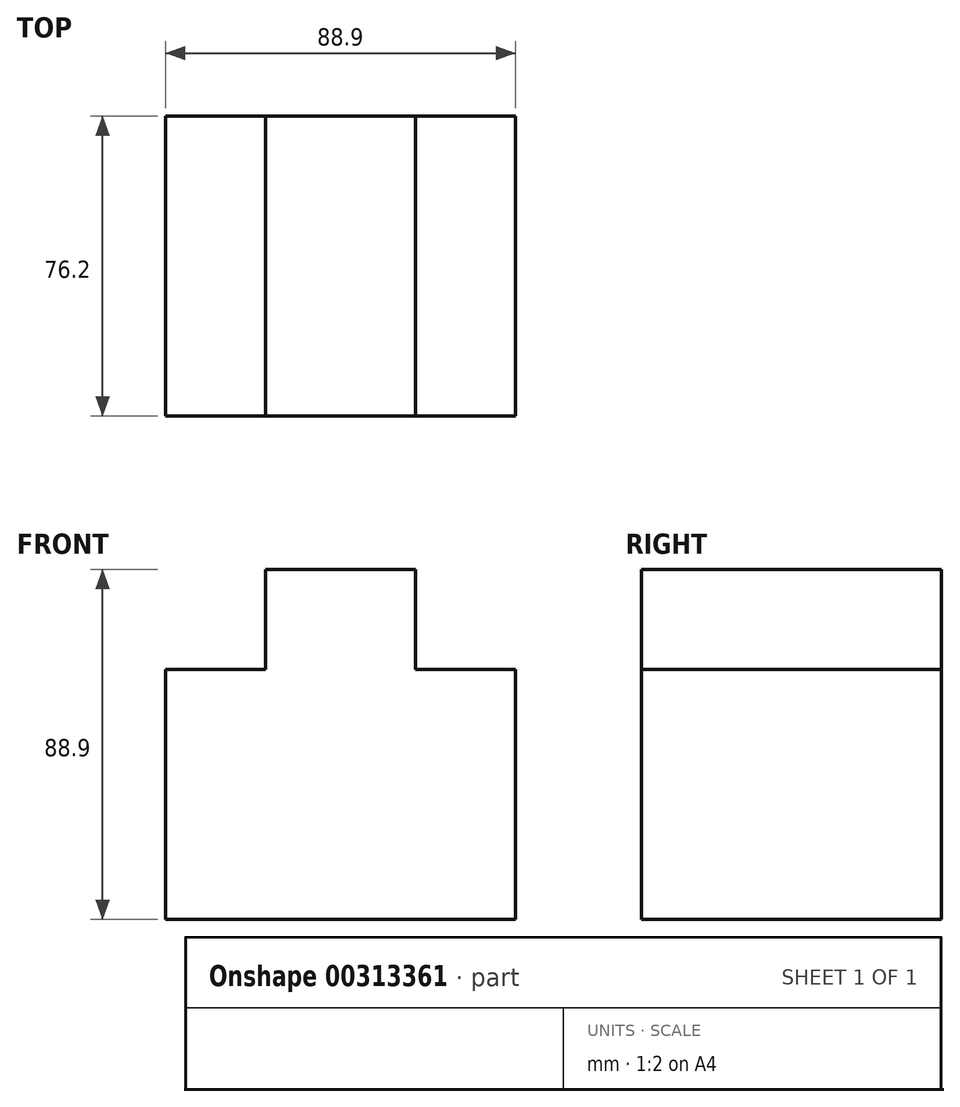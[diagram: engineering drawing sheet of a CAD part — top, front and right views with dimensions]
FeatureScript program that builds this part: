
annotation { "Feature Type Name" : "Feature", "Feature Type Description" : "" }
export const myFeature = defineFeature(function(context is Context, id is Id, definition is map)
    precondition{}
    {
        {
            var Q0;
            Q0=qCreatedBy(makeId("Front.planeOp"),FACE);
            var sketch = newSketch(context, id + "F0", { "sketchPlane" : qUnion([Q0])});
            skLineSegment(sketch, "E0", {"start": v(-46.42, -47.97) * mm, "end": v(42.48, -47.97) * mm});
            skLineSegment(sketch, "E1", {"start": v(42.48, -47.97) * mm, "end": v(42.48, 15.53) * mm});
            skLineSegment(sketch, "E2", {"start": v(42.48, 15.53) * mm, "end": v(17.08, 15.53) * mm});
            skLineSegment(sketch, "E3", {"start": v(17.08, 15.53) * mm, "end": v(17.08, 40.93) * mm});
            skLineSegment(sketch, "E4", {"start": v(17.08, 40.93) * mm, "end": v(-21.02, 40.93) * mm});
            skLineSegment(sketch, "E5", {"start": v(-21.02, 40.93) * mm, "end": v(-21.02, 15.53) * mm});
            skLineSegment(sketch, "E6", {"start": v(-21.02, 15.53) * mm, "end": v(-46.42, 15.53) * mm});
            skLineSegment(sketch, "E7", {"start": v(-46.42, 15.53) * mm, "end": v(-46.42, -47.97) * mm});
            skSolve(sketch);
        }
        {
            var Q0;
            Q0=makeQuery(id+"F0.imprint","IMPRINT",FACE,{"disambiguationData":[TD([[makeQuery(id+"F0.imprint","IMPRINT",EDGE,{"derivedFrom":sQuery(id+"F0.wireOp",EDGE,"E0")}),1.0]])]});
            extrude(context, id + "F1", {"entities" : qUnion([Q0]), "depth" : 76.2 * mm});
        }
    });
